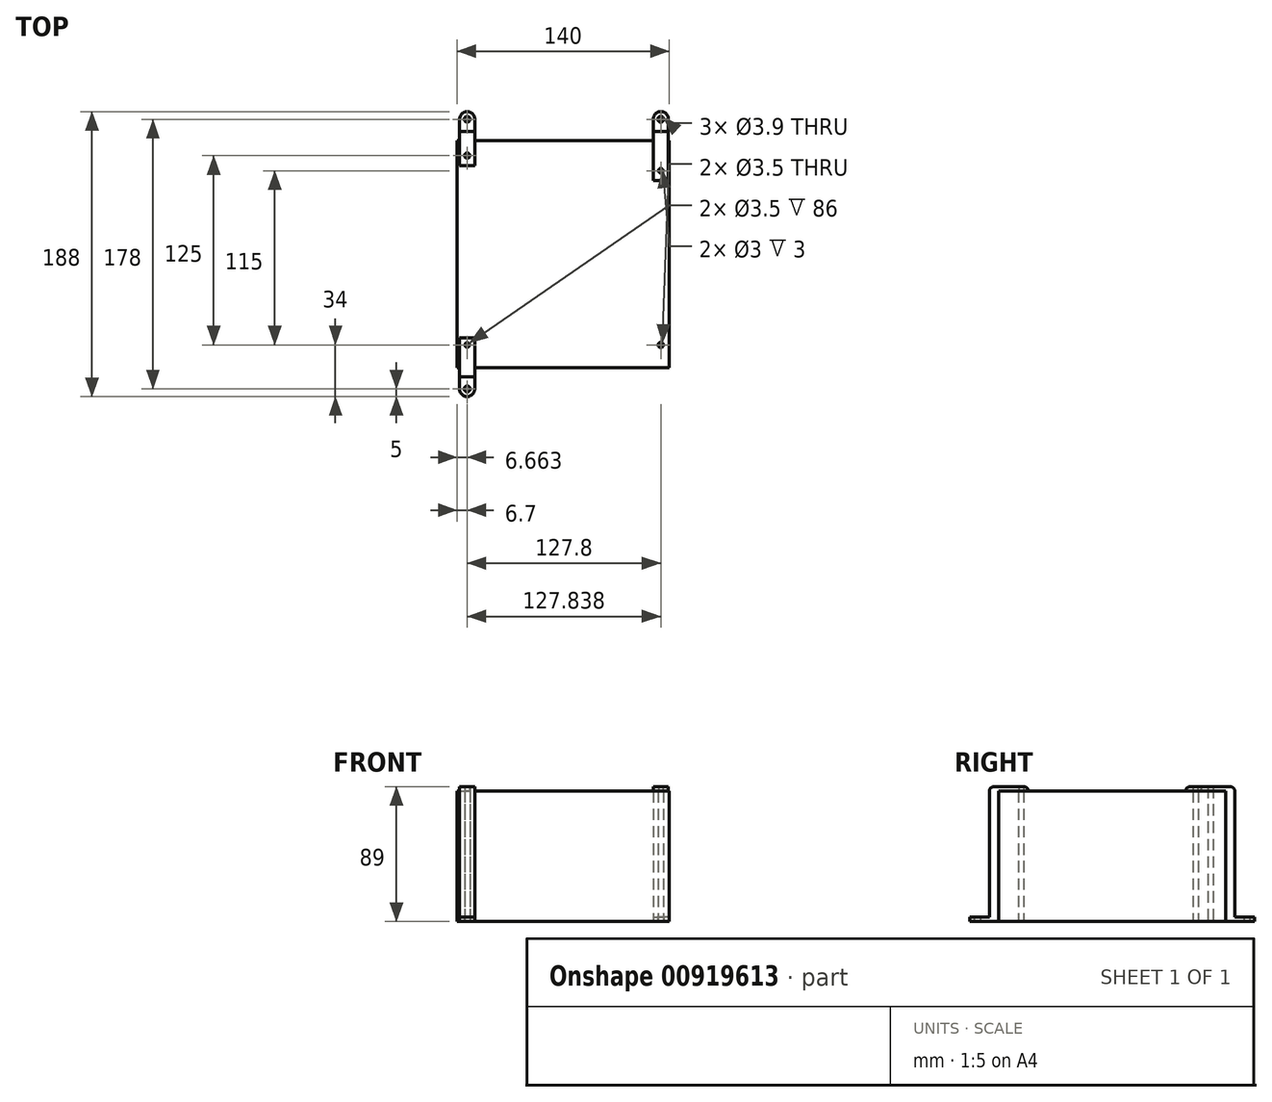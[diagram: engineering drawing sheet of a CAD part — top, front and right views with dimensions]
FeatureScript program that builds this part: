
annotation { "Feature Type Name" : "Feature", "Feature Type Description" : "" }
export const myFeature = defineFeature(function(context is Context, id is Id, definition is map)
    precondition{}
    {
        {
            var Q0;
            Q0=qCreatedBy(makeId("Top.planeOp"),FACE);
            var sketch = newSketch(context, id + "F0", { "sketchPlane" : qUnion([Q0])});
            skLineSegment(sketch, "E0.rect.bottom", {"start": v(70, -75) * mm, "end": v(-70, -75) * mm});
            skLineSegment(sketch, "E0.rect.top", {"start": v(70, 75) * mm, "end": v(-70, 75) * mm});
            skLineSegment(sketch, "E0.rect.left", {"start": v(70, -75) * mm, "end": v(70, 75) * mm});
            skLineSegment(sketch, "E0.rect.right", {"start": v(-70, -75) * mm, "end": v(-70, 75) * mm});
            skPoint(sketch, "E0.rect.middle", {"position": v(0, 0) * mm});
            skCircle(sketch, "E1", {"center": v(-63.3, 65) * mm, "radius": 1.75 * mm});
            skCircle(sketch, "E2", {"center": v(64.5, 55) * mm, "radius": 1.75 * mm});
            skCircle(sketch, "E3", {"center": v(64.5, -60) * mm, "radius": 1.75 * mm});
            skCircle(sketch, "E4", {"center": v(-63.3, -60) * mm, "radius": 1.75 * mm});
            skSolve(sketch);
        }
        {
            var Q0;
            Q0=qSketchRegion(id+"F0",true);
            extrude(context, id + "F1", {"entities" : qUnion([Q0]), "depth" : 86 * mm});
        }
        {
            var Q0;
            Q0=qCreatedBy(makeId("Top.planeOp"),FACE);
            var sketch = newSketch(context, id + "F2", { "sketchPlane" : qUnion([Q0])});
            skCircle(sketch, "E5", {"center": v(-63.3, 89) * mm, "radius": 1.95 * mm});
            skCircle(sketch, "E6", {"center": v(-63.3, 89) * mm, "radius": 5 * mm});
            skLineSegment(sketch, "E7.bottom", {"start": v(-68.3, 75) * mm, "end": v(-58.3, 75) * mm});
            skLineSegment(sketch, "E7.top", {"start": v(-68.3, 81) * mm, "end": v(-58.3, 81) * mm});
            skLineSegment(sketch, "E7.left", {"start": v(-68.3, 75) * mm, "end": v(-68.3, 81) * mm});
            skLineSegment(sketch, "E7.right", {"start": v(-58.3, 75) * mm, "end": v(-58.3, 81) * mm});
            skLineSegment(sketch, "E8", {"start": v(-63.3, 98.83) * mm, "end": v(-63.3, 65) * mm, "construction": true});
            skLineSegment(sketch, "E9", {"start": v(-68.3, 81) * mm, "end": v(-68.3, 89) * mm});
            skLineSegment(sketch, "E10", {"start": v(-58.3, 81) * mm, "end": v(-58.3, 89) * mm});
            skSolve(sketch);
        }
        {
            var Q0;
            Q0=makeQuery(id+"F2.imprint","IMPRINT",FACE,{"disambiguationData":[TD([[makeQuery(id+"F2.imprint","IMPRINT",EDGE,{"derivedFrom":sQuery(id+"F2.wireOp",EDGE,"E5")}),-1.0]])]});
            var Q1;
            Q1=makeQuery(id+"F2.imprint","IMPRINT",FACE,{"disambiguationData":[TD([[makeQuery(id+"F2.imprint","IMPRINT",EDGE,{"derivedFrom":sQuery(id+"F2.wireOp",EDGE,"E7.top")}),1.0]])]});
            extrude(context, id + "F3", {"entities" : qUnion([Q0, Q1]), "depth" : 3 * mm});
        }
        {
            var Q0;
            Q0=makeQuery(id+"F2.imprint","IMPRINT",FACE,{"disambiguationData":[TD([[makeQuery(id+"F2.imprint","IMPRINT",EDGE,{"derivedFrom":sQuery(id+"F2.wireOp",EDGE,"E7.bottom")}),1.0]])]});
            extrude(context, id + "F4", {"entities" : qUnion([Q0]), "operationType" : NewBodyOperationType.ADD, "depth" : 86 * mm});
        }
        {
            var Q0;
            Q0=makeQuery(id+"F4.opExtrude","CAP_FACE",FACE,{"disambiguationData":[OSD([sQuery(id+"F2.wireOp",EDGE,"E7.bottom"),sQuery(id+"F2.wireOp",EDGE,"E7.top"),sQuery(id+"F2.wireOp",EDGE,"E7.left"),sQuery(id+"F2.wireOp",EDGE,"E7.right")])],"isStart":false});
            var sketch = newSketch(context, id + "F5", { "sketchPlane" : qUnion([Q0])});
            skLineSegment(sketch, "E11.bottom", {"start": v(-68.3, 81) * mm, "end": v(-58.3, 81) * mm});
            skLineSegment(sketch, "E11.top", {"start": v(-68.3, 58.38) * mm, "end": v(-58.3, 58.38) * mm});
            skLineSegment(sketch, "E11.left", {"start": v(-68.3, 81) * mm, "end": v(-68.3, 58.38) * mm});
            skLineSegment(sketch, "E11.right", {"start": v(-58.3, 81) * mm, "end": v(-58.3, 58.38) * mm});
            skCircle(sketch, "E12", {"center": v(-63.3, 65) * mm, "radius": 1.5 * mm});
            skSolve(sketch);
        }
        {
            var Q0;
            {var subQ2=sQuery(id+"F5.wireOp",EDGE,"E11.top");Q0=makeQuery(id+"F5.imprint","IMPRINT",FACE,{"disambiguationData":[TD([[makeQuery(id+"F5.imprint","IMPRINT",EDGE,{"derivedFrom":subQ2}),1.0]])]});}
            var Q1;
            {var subQ2=sQuery(id+"F5.wireOp",EDGE,"E11.bottom");Q1=makeQuery(id+"F5.imprint","IMPRINT",FACE,{"disambiguationData":[TD([[makeQuery(id+"F5.imprint","IMPRINT",EDGE,{"derivedFrom":subQ2}),-1.0]])]});}
            extrude(context, id + "F6", {"entities" : qUnion([Q0, Q1]), "operationType" : NewBodyOperationType.ADD, "depth" : 3 * mm});
        }
        {
            var Q0;
            Q0=qCreatedBy(makeId("Top.planeOp"),FACE);
            var sketch = newSketch(context, id + "F7", { "sketchPlane" : qUnion([Q0])});
            skCircle(sketch, "E13", {"center": v(64.5, 89) * mm, "radius": 1.95 * mm});
            skCircle(sketch, "E14", {"center": v(64.5, 89) * mm, "radius": 5 * mm});
            skLineSegment(sketch, "E15.bottom", {"start": v(59.5, 75) * mm, "end": v(69.5, 75) * mm});
            skLineSegment(sketch, "E15.top", {"start": v(59.5, 81) * mm, "end": v(69.5, 81) * mm});
            skLineSegment(sketch, "E15.left", {"start": v(59.5, 75) * mm, "end": v(59.5, 81) * mm});
            skLineSegment(sketch, "E15.right", {"start": v(69.5, 75) * mm, "end": v(69.5, 81) * mm});
            skLineSegment(sketch, "E16", {"start": v(64.5, 98.83) * mm, "end": v(64.5, 65) * mm, "construction": true});
            skLineSegment(sketch, "E17", {"start": v(59.5, 81) * mm, "end": v(59.5, 89) * mm});
            skLineSegment(sketch, "E18", {"start": v(69.5, 81) * mm, "end": v(69.5, 89) * mm});
            skSolve(sketch);
        }
        {
            var Q0;
            Q0=makeQuery(id+"F7.imprint","IMPRINT",FACE,{"disambiguationData":[TD([[makeQuery(id+"F7.imprint","IMPRINT",EDGE,{"derivedFrom":sQuery(id+"F7.wireOp",EDGE,"E13")}),-1.0]])]});
            var Q1;
            Q1=makeQuery(id+"F7.imprint","IMPRINT",FACE,{"disambiguationData":[TD([[makeQuery(id+"F7.imprint","IMPRINT",EDGE,{"derivedFrom":sQuery(id+"F7.wireOp",EDGE,"E15.top")}),1.0]])]});
            extrude(context, id + "F8", {"entities" : qUnion([Q0, Q1]), "depth" : 3 * mm});
        }
        {
            var Q0;
            Q0=makeQuery(id+"F7.imprint","IMPRINT",FACE,{"disambiguationData":[TD([[makeQuery(id+"F7.imprint","IMPRINT",EDGE,{"derivedFrom":sQuery(id+"F7.wireOp",EDGE,"E15.bottom")}),1.0]])]});
            extrude(context, id + "F9", {"entities" : qUnion([Q0]), "operationType" : NewBodyOperationType.ADD, "depth" : 86 * mm});
        }
        {
            var Q0;
            Q0=makeQuery(id+"F9.opExtrude","CAP_FACE",FACE,{"disambiguationData":[OSD([sQuery(id+"F7.wireOp",EDGE,"E15.bottom"),sQuery(id+"F7.wireOp",EDGE,"E15.top"),sQuery(id+"F7.wireOp",EDGE,"E15.left"),sQuery(id+"F7.wireOp",EDGE,"E15.right")])],"isStart":false});
            var sketch = newSketch(context, id + "F10", { "sketchPlane" : qUnion([Q0])});
            skLineSegment(sketch, "E19.bottom", {"start": v(59.5, 81) * mm, "end": v(69.5, 81) * mm});
            skLineSegment(sketch, "E19.top", {"start": v(59.5, 48.52) * mm, "end": v(69.5, 48.52) * mm});
            skLineSegment(sketch, "E19.left", {"start": v(59.5, 81) * mm, "end": v(59.5, 48.52) * mm});
            skLineSegment(sketch, "E19.right", {"start": v(69.5, 81) * mm, "end": v(69.5, 48.52) * mm});
            skCircle(sketch, "E20", {"center": v(64.5, 55) * mm, "radius": 1.5 * mm});
            skSolve(sketch);
        }
        {
            var Q0;
            Q0=qSketchRegion(id+"F10",true);
            extrude(context, id + "F11", {"entities" : qUnion([Q0]), "operationType" : NewBodyOperationType.ADD, "depth" : 3 * mm});
        }
        {
            var Q0;
            Q0=qCreatedBy(makeId("Top.planeOp"),FACE);
            var sketch = newSketch(context, id + "F12", { "sketchPlane" : qUnion([Q0])});
            skCircle(sketch, "E21", {"center": v(-63.34, -89) * mm, "radius": 1.95 * mm});
            skCircle(sketch, "E22", {"center": v(-63.34, -89) * mm, "radius": 5 * mm});
            skLineSegment(sketch, "E23.bottom", {"start": v(-68.34, -75) * mm, "end": v(-58.34, -75) * mm});
            skLineSegment(sketch, "E23.top", {"start": v(-68.34, -81) * mm, "end": v(-58.34, -81) * mm});
            skLineSegment(sketch, "E23.left", {"start": v(-68.34, -81) * mm, "end": v(-68.34, -75) * mm});
            skLineSegment(sketch, "E23.right", {"start": v(-58.34, -81) * mm, "end": v(-58.34, -75) * mm});
            skLineSegment(sketch, "E24", {"start": v(-63.34, -31.67) * mm, "end": v(-63.34, -61.75) * mm, "construction": true});
            skLineSegment(sketch, "E25", {"start": v(-68.34, -89) * mm, "end": v(-68.34, -81) * mm});
            skLineSegment(sketch, "E26", {"start": v(-58.34, -89) * mm, "end": v(-58.34, -81) * mm});
            skSolve(sketch);
        }
        {
            var Q0;
            Q0=makeQuery(id+"F12.imprint","IMPRINT",FACE,{"disambiguationData":[TD([[makeQuery(id+"F12.imprint","IMPRINT",EDGE,{"derivedFrom":sQuery(id+"F12.wireOp",EDGE,"E23.bottom")}),-1.0]])]});
            extrude(context, id + "F13", {"entities" : qUnion([Q0]), "depth" : 86 * mm});
        }
        {
            var Q0;
            Q0=makeQuery(id+"F12.imprint","IMPRINT",FACE,{"disambiguationData":[TD([[makeQuery(id+"F12.imprint","IMPRINT",EDGE,{"derivedFrom":sQuery(id+"F12.wireOp",EDGE,"E23.top")}),-1.0]])]});
            var Q1;
            Q1=makeQuery(id+"F12.imprint","IMPRINT",FACE,{"disambiguationData":[TD([[makeQuery(id+"F12.imprint","IMPRINT",EDGE,{"derivedFrom":sQuery(id+"F12.wireOp",EDGE,"E21")}),-1.0]])]});
            extrude(context, id + "F14", {"entities" : qUnion([Q0, Q1]), "operationType" : NewBodyOperationType.ADD, "depth" : 3 * mm});
        }
        {
            var Q0;
            Q0=makeQuery(id+"F13.opExtrude","CAP_FACE",FACE,{"disambiguationData":[OSD([sQuery(id+"F12.wireOp",EDGE,"E23.bottom"),sQuery(id+"F12.wireOp",EDGE,"E23.top"),sQuery(id+"F12.wireOp",EDGE,"E23.left"),sQuery(id+"F12.wireOp",EDGE,"E23.right")])],"isStart":false});
            var sketch = newSketch(context, id + "F15", { "sketchPlane" : qUnion([Q0])});
            skLineSegment(sketch, "E27.bottom", {"start": v(-68.34, -55.23) * mm, "end": v(-58.34, -55.23) * mm});
            skLineSegment(sketch, "E27.top", {"start": v(-68.34, -81) * mm, "end": v(-58.34, -81) * mm});
            skLineSegment(sketch, "E27.left", {"start": v(-68.34, -55.23) * mm, "end": v(-68.34, -81) * mm});
            skLineSegment(sketch, "E27.right", {"start": v(-58.34, -55.23) * mm, "end": v(-58.34, -81) * mm});
            skCircle(sketch, "E28", {"center": v(-63.3, -60) * mm, "radius": 1.5 * mm});
            skSolve(sketch);
        }
        {
            var Q0;
            Q0=qSketchRegion(id+"F15",true);
            extrude(context, id + "F16", {"entities" : qUnion([Q0]), "operationType" : NewBodyOperationType.ADD, "depth" : 3 * mm});
        }
        {
            var Q0;
            Q0=makeQuery(id+"F11.opExtrude","CAP_EDGE",EDGE,{"disambiguationData":[OSD([sQuery(id+"F10.wireOp",EDGE,"E19.bottom")])],"isStart":false});
            var Q1;
            Q1=makeQuery(id+"F6.opExtrude","CAP_EDGE",EDGE,{"disambiguationData":[OSD([sQuery(id+"F5.wireOp",EDGE,"E11.bottom")])],"isStart":false});
            var Q2;
            Q2=makeQuery(id+"F8.opExtrude","CAP_EDGE",EDGE,{"disambiguationData":[OSD([sQuery(id+"F7.wireOp",EDGE,"E15.top")])],"isStart":false});
            var Q3;
            Q3=makeQuery(id+"F3.opExtrude","CAP_EDGE",EDGE,{"disambiguationData":[OSD([sQuery(id+"F2.wireOp",EDGE,"E7.top")])],"isStart":false});
            var Q4;
            Q4=makeQuery(id+"F11.opExtrude","CAP_EDGE",EDGE,{"disambiguationData":[OSD([sQuery(id+"F10.wireOp",EDGE,"E19.top")])],"isStart":false});
            var Q5;
            Q5=makeQuery(id+"F6.opExtrude","CAP_EDGE",EDGE,{"disambiguationData":[OSD([sQuery(id+"F5.wireOp",EDGE,"E11.top")])],"isStart":false});
            var Q6;
            Q6=makeQuery(id+"F16.opExtrude","CAP_EDGE",EDGE,{"disambiguationData":[OSD([sQuery(id+"F15.wireOp",EDGE,"E27.top")])],"isStart":false});
            var Q7;
            Q7=makeQuery(id+"F16.opExtrude","CAP_EDGE",EDGE,{"disambiguationData":[OSD([sQuery(id+"F15.wireOp",EDGE,"E27.bottom")])],"isStart":false});
            var Q8;
            Q8=makeQuery(id+"F14.opExtrude","CAP_EDGE",EDGE,{"disambiguationData":[OSD([sQuery(id+"F12.wireOp",EDGE,"E23.top")])],"isStart":false});
            fillet(context, id + "F17", {"entities" : qUnion([Q0, Q1, Q2, Q3, Q4, Q5, Q6, Q7, Q8]), "radius" : 3 * mm, "tangentPropagation" : true, "allowEdgeOverflow" : false});
        }
    });
